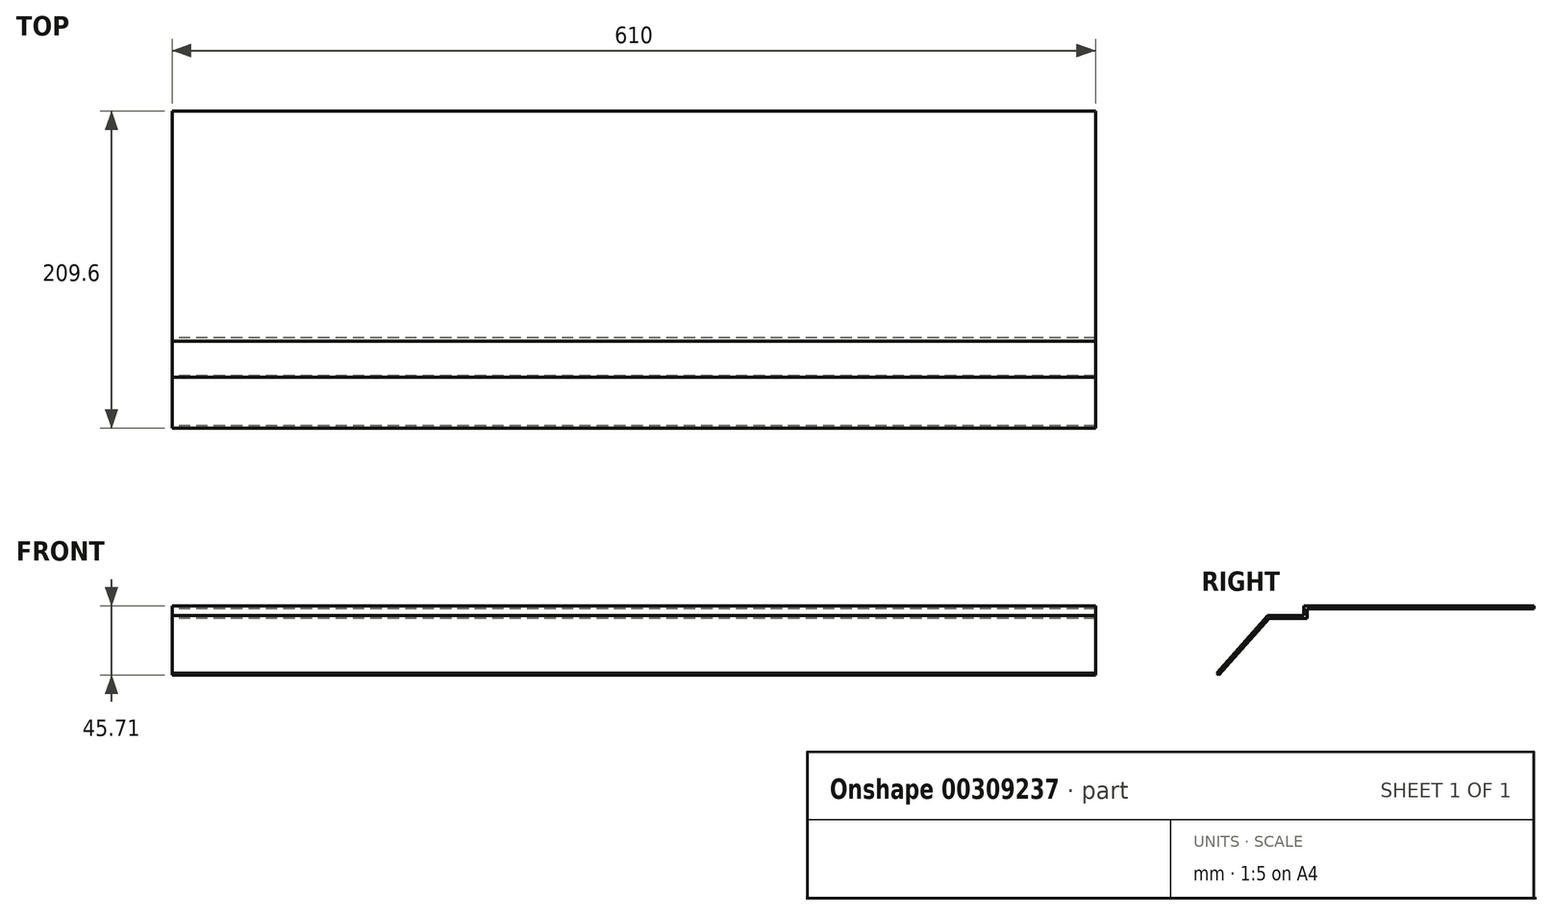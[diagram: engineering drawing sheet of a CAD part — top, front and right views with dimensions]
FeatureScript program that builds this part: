
annotation { "Feature Type Name" : "Feature", "Feature Type Description" : "" }
export const myFeature = defineFeature(function(context is Context, id is Id, definition is map)
    precondition{}
    {
        {
            var Q0;
            Q0=qCreatedBy(makeId("Right.planeOp"),FACE);
            var sketch = newSketch(context, id + "F0", { "sketchPlane" : qUnion([Q0])});
            skLineSegment(sketch, "E0", {"start": v(0, 0) * mm, "end": v(-150, 0) * mm});
            skLineSegment(sketch, "E1", {"start": v(-150, 0) * mm, "end": v(-150, -6.23) * mm});
            skLineSegment(sketch, "E2", {"start": v(-150, -6.23) * mm, "end": v(-175, -6.23) * mm});
            skLineSegment(sketch, "E3", {"start": v(-175, -6.23) * mm, "end": v(-208.1, -43.71) * mm});
            skLineSegment(sketch, "E4.0", {"start": v(-175.9, -4.23) * mm, "end": v(-209.6, -42.39) * mm});
            skLineSegment(sketch, "E4.1", {"start": v(-152, -4.23) * mm, "end": v(-175.9, -4.23) * mm});
            skLineSegment(sketch, "E4.2", {"start": v(-152, 2) * mm, "end": v(-152, -4.23) * mm});
            skLineSegment(sketch, "E4.3", {"start": v(0, 2) * mm, "end": v(-152, 2) * mm});
            skLineSegment(sketch, "E5", {"start": v(0, 0) * mm, "end": v(0, 2) * mm});
            skLineSegment(sketch, "E6", {"start": v(-208.1, -43.71) * mm, "end": v(-209.6, -42.39) * mm});
            skSolve(sketch);
        }
        {
            var Q0;
            Q0=makeQuery(id+"F0.imprint","IMPRINT",FACE,{"disambiguationData":[TD([[makeQuery(id+"F0.imprint","IMPRINT",EDGE,{"derivedFrom":sQuery(id+"F0.wireOp",EDGE,"E0")}),-1.0]])]});
            extrude(context, id + "F1", {"entities" : qUnion([Q0]), "depth" : 610 * mm});
        }
    });
